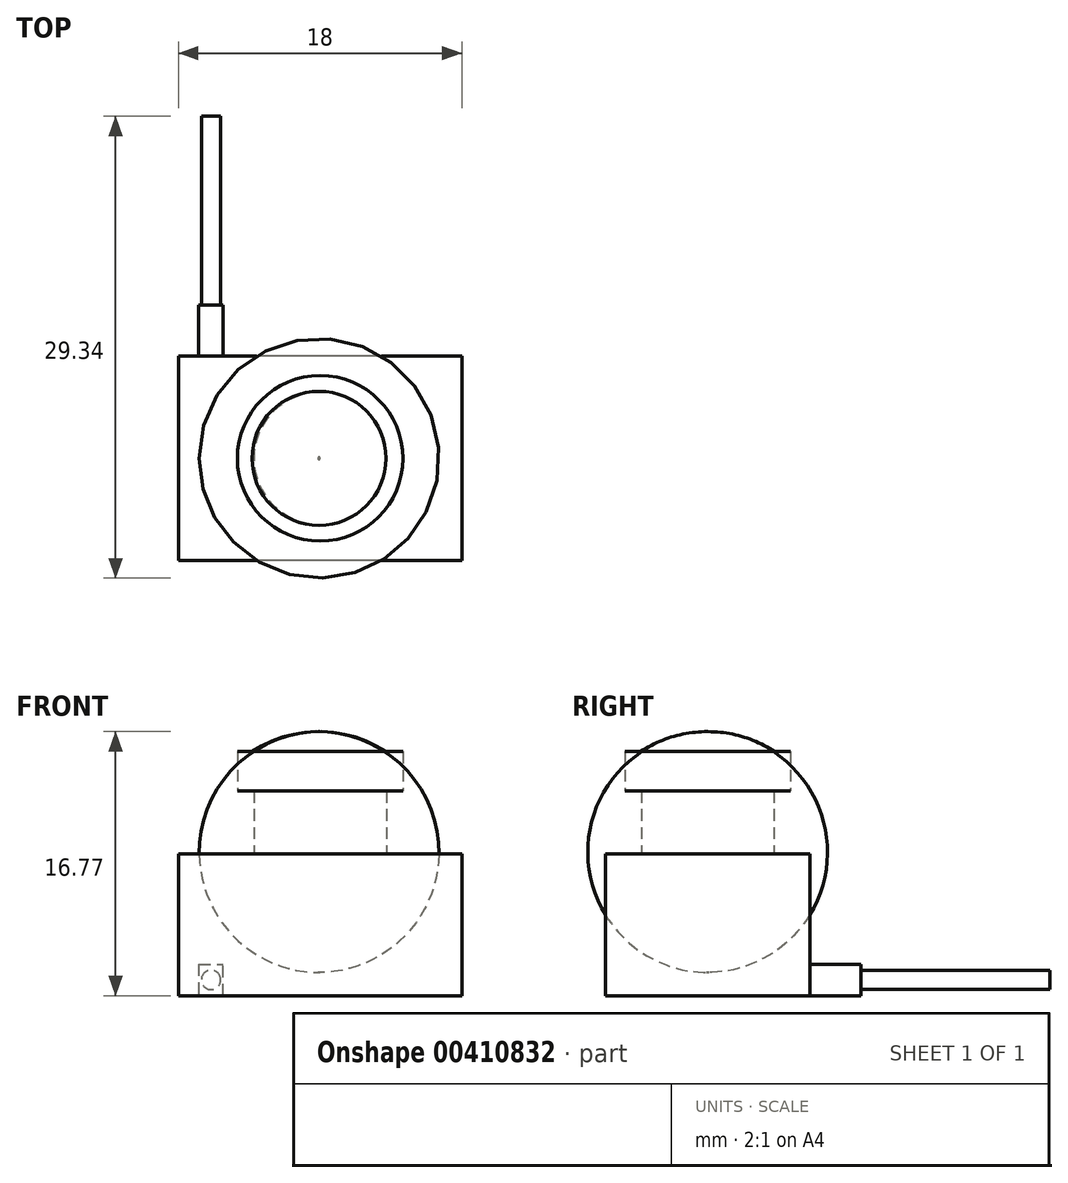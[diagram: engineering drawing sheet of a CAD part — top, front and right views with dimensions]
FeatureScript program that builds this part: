
annotation { "Feature Type Name" : "Feature", "Feature Type Description" : "" }
export const myFeature = defineFeature(function(context is Context, id is Id, definition is map)
    precondition{}
    {
        {
            var Q0;
            Q0=qCreatedBy(makeId("Top.planeOp"),FACE);
            var sketch = newSketch(context, id + "F0", { "sketchPlane" : qUnion([Q0])});
            skLineSegment(sketch, "E0.bottom", {"start": v(9, 6.5) * mm, "end": v(-9, 6.5) * mm});
            skLineSegment(sketch, "E0.top", {"start": v(9, -6.5) * mm, "end": v(-9, -6.5) * mm});
            skLineSegment(sketch, "E0.left", {"start": v(9, 6.5) * mm, "end": v(9, -6.5) * mm});
            skLineSegment(sketch, "E0.right", {"start": v(-9, 6.5) * mm, "end": v(-9, -6.5) * mm});
            skPoint(sketch, "E0.middle", {"position": v(0, 0) * mm});
            skSolve(sketch);
        }
        {
            var Q0;
            Q0 = qSketchRegion(id + "F0", true);
            extrude(context, id + "F1", {"entities" : qUnion([Q0]), "depth" : 9 * mm});
        }
        {
            var Q0;
            Q0=makeQuery(id+"F1.opExtrude","CAP_FACE",FACE,{"disambiguationData":[OSD([sQuery(id+"F0.wireOp",EDGE,"E0.bottom"),sQuery(id+"F0.wireOp",EDGE,"E0.top"),sQuery(id+"F0.wireOp",EDGE,"E0.left"),sQuery(id+"F0.wireOp",EDGE,"E0.right")])],"isStart":false});
            var sketch = newSketch(context, id + "F2", { "sketchPlane" : qUnion([Q0])});
            skCircle(sketch, "E1", {"center": v(0, 0) * mm, "radius": 4.2 * mm});
            skSolve(sketch);
        }
        {
            var Q0;
            Q0 = qSketchRegion(id + "F2", true);
            extrude(context, id + "F3", {"entities" : qUnion([Q0]), "operationType" : NewBodyOperationType.ADD, "depth" : 4 * mm});
        }
        {
            var Q0;
            Q0=makeQuery(id+"F3.opExtrude","CAP_FACE",FACE,{"disambiguationData":[OSD([sQuery(id+"F2.wireOp",EDGE,"E1")])],"isStart":false});
            var sketch = newSketch(context, id + "F4", { "sketchPlane" : qUnion([Q0])});
            skCircle(sketch, "E2", {"center": v(0, 0) * mm, "radius": 5.26 * mm});
            skSolve(sketch);
        }
        {
            var Q0;
            Q0 = qSketchRegion(id + "F4", true);
            extrude(context, id + "F5", {"entities" : qUnion([Q0]), "operationType" : NewBodyOperationType.ADD, "depth" : 2.5 * mm});
        }
        {
            var Q0;
            Q0=makeQuery(id+"F1.opExtrude","CAP_FACE",FACE,{"disambiguationData":[OSD([sQuery(id+"F0.wireOp",EDGE,"E0.bottom"),sQuery(id+"F0.wireOp",EDGE,"E0.top"),sQuery(id+"F0.wireOp",EDGE,"E0.left"),sQuery(id+"F0.wireOp",EDGE,"E0.right")])],"isStart":true});
            var sketch = newSketch(context, id + "F6", { "sketchPlane" : qUnion([Q0])});
            skLineSegment(sketch, "E3", {"start": v(-7.7, -4.94) * mm, "end": v(-7.7, -9.73) * mm});
            skLineSegment(sketch, "E4", {"start": v(-7.7, -9.73) * mm, "end": v(-6.15, -9.73) * mm});
            skLineSegment(sketch, "E5", {"start": v(-6.15, -9.73) * mm, "end": v(-6.15, -4.97) * mm});
            skLineSegment(sketch, "E6", {"start": v(-6.15, -4.97) * mm, "end": v(-7.7, -4.94) * mm});
            skSolve(sketch);
        }
        {
            var Q0;
            Q0 = qSketchRegion(id + "F6", true);
            extrude(context, id + "F7", {"entities" : qUnion([Q0]), "operationType" : NewBodyOperationType.ADD, "oppositeDirection" : true, "depth" : 2 * mm});
        }
        {
            var Q0;
            Q0=makeQuery(id+"F7.opExtrude","SWEPT_FACE",FACE,{"disambiguationData":[OSD([sQuery(id+"F6.wireOp",EDGE,"E4")])]});
            var sketch = newSketch(context, id + "F8", { "sketchPlane" : qUnion([Q0])});
            skCircle(sketch, "E7", {"center": v(6.93, 1) * mm, "radius": 0.61 * mm});
            skSolve(sketch);
        }
        {
            var Q0;
            Q0 = qSketchRegion(id + "F8", true);
            extrude(context, id + "F9", {"entities" : qUnion([Q0]), "operationType" : NewBodyOperationType.ADD, "depth" : 12 * mm});
        }
        {
            var Q0;
            Q0=qCreatedBy(makeId("Front.planeOp"),FACE);
            var sketch = newSketch(context, id + "F10", { "sketchPlane" : qUnion([Q0])});
            skArc(sketch, "E8", {"start": v(4.4, 15.35) * mm, "mid": v(2.28, 16.41) * mm, "end": v(-0.07, 16.77) * mm});
            skLineSegment(sketch, "E9", {"start": v(-0.07, 16.77) * mm, "end": v(-0.07, 14.75) * mm});
            skPoint(sketch, "E9.endSnap0", {"position": v(-0.07, 16.77) * mm});
            skLineSegment(sketch, "E10", {"start": v(-0.07, 14.75) * mm, "end": v(4.4, 14.75) * mm});
            skLineSegment(sketch, "E11", {"start": v(4.4, 14.75) * mm, "end": v(4.4, 15.35) * mm});
            skSolve(sketch);
        }
        {
            var Q0;
            Q0 = qSketchRegion(id + "F10", true);
            var Q1;
            Q1=sQuery(id+"F10.wireOp",EDGE,"E9");
            revolve(context, id + "F11", {"operationType" : NewBodyOperationType.ADD, "entities" : qUnion([Q0]), "axis" : qUnion([Q1]), "revolveType" : RevolveType.FULL});
        }
    });
